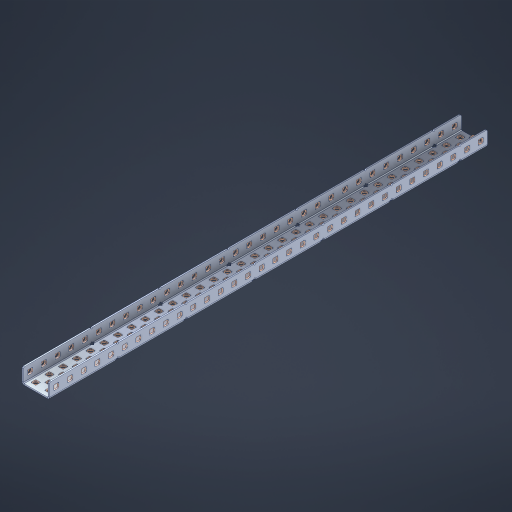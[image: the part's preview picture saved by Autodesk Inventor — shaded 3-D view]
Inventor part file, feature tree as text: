
AUTODESK INVENTOR PART (.ipt)
format: ipt  version: 2023 (Build 270158000, 158)  size: 1,968,128 bytes
history: native  units: in
note: dims shown in document units (in); Inventor stores cm internally (conversion verified against a paired STEP export)
features: other x167, extrude x158, sheet_metal_op x11, sketch x10, pattern_linear x2, mirror x1, chamfer x1
ambient origin geometry x8: Origin, YZ Plane, XZ Plane, XY Plane, X Axis, Y Axis, Z Axis, Center Point
bodies: Solid1 (feature_tree), Body (feature_tree)
feature tree (350):
  sheet_metal_op  "Flanges"
  other  "Flange Pattern Plane"
  other  "Flange Pattern Sketch"
  sheet_metal_op  "Flange Pattern"
  sheet_metal_op  "Body Pattern"
  pattern_linear  "Center Pattern"  Spacing1=0.0469in  [1 undecoded]
  other  "Arc Length"
  mirror  "Notch Mirror"
  pattern_linear  "Notch Pattern"  Spacing1=0.182in  [1 undecoded]
  chamfer  "End Chamfer"
  extrude  "Half Cut"  Depth=0.02in
  sketch  "Sketch1"  dims[d0=1.0in]
  other  "Plate1"
  sketch  "Sketch2"  dims[d1=16.0in]
  other  "Plate2"
  sheet_metal_op  "Bend1"
  sheet_metal_op  "Corner1"
  sketch  "Sketch3"  dims[d2=0.0469in]
  sketch  "Sketch7"  dims[d3=0.0469in]
  other  "Srf1"
  other  "Srf2"
  sketch  "Sketch8"  dims[d4=0.0234in]
  sketch  "Sketch9"  dims[d5=0.0938in]
  other  "Srf91"
  sheet_metal_op  "Body Pattern Sketch"
  other  "Srf92"
  sketch  "Sketch13"  dims[d6=0.0469in]
  sketch  "Sketch14"  dims[d7=0.5in d8=90.0deg d9=0.0312in]
  sketch  "Sketch15"  dims[d10=0.1875in]
  sketch  "Sketch16"  dims[d11=0.0469in d12=0.0469in d16=0.182in d17=0.02in d18=0.0469in d19=0.0in d20=0.25in d21=0.25in d38=12.5984in d40=0.5in d41=0.7874in d43=1.0in d46=0.172in d47=1.0in d48=0.0in d49=0.182in d50=0.02in d51=0.25in d52=0.25in d53=0.0469in d54=0.0in d55=0.172in d56=1.0in d57=0.0in d58=0.25in d60=12.5984in d62=0.5in d63=0.7874in d65=0.5in d85=0.1227in d86=0.1659in d88=0.04in d89=0.0469in d90=0.0in d91=0.04in d92=0.0491in d95=2.5in d96=0.04in d97=0.25in d98=45.0deg d99=0.25in d100=0.5in d101=0.0in d102=2.497in d106=0.182in d107=0.02in d108=0.5in d109=0.5in d110=0.0469in d111=0.0in d112=0.172in d113=0.5in d114=0.0in d117=0.5in d118=0.5in d119=0.5in]
  other  "Srf786"
  other  "Srf823"
  other  "Srf824"
  other  "Srf825"
  other  "Srf826"
  other  "Srf827"
  other  "Srf828"
  other  "Srf829"
  other  "Srf856"
  other  "Srf857"
  other  "Srf858"
  other  "Srf859"
  other  "Srf860"
  other  "Srf861"
  other  "Srf862"
  other  "Srf889"
  other  "Srf890"
  other  "Srf891"
  other  "Srf892"
  other  "Srf893"
  other  "Srf894"
  other  "Srf895"
  other  "Srf896"
  other  "Srf922"
  other  "Srf923"
  other  "Srf924"
  other  "Srf925"
  other  "Srf926"
  other  "Srf959"
  other  "Srf960"
  other  "Srf961"
  other  "Srf962"
  other  "Srf963"
  other  "Srf996"
  other  "Srf997"
  other  "Srf998"
  other  "Srf999"
  other  "Srf1000"
  other  "Srf1143"
  other  "Srf1144"
  other  "Srf1145"
  other  "Srf1146"
  other  "Srf1147"
  other  "Srf1148"
  other  "Srf1149"
  other  "Srf1150"
  other  "Srf1151"
  other  "Srf1152"
  other  "Srf1153"
  other  "Srf1154"
  other  "Srf1155"
  other  "Srf1156"
  other  "Srf1157"
  other  "Srf1158"
  other  "Srf1159"
  other  "Srf1160"
  other  "Srf1161"
  other  "Srf1162"
  other  "Srf1163"
  other  "Srf1164"
  other  "Srf1165"
  other  "Srf1166"
  other  "Srf1167"
  other  "Srf1168"
  other  "Srf1169"
  other  "Srf1170"
  other  "Srf1171"
  other  "Srf1172"
  other  "Srf1173"
  other  "Srf1174"
  other  "Srf1175"
  other  "Srf1176"
  other  "Srf1177"
  other  "Srf1178"
  other  "Srf1179"
  other  "Srf1180"
  other  "Srf1181"
  other  "Srf1182"
  other  "Srf1183"
  other  "Srf1184"
  other  "Srf1185"
  other  "Srf1186"
  other  "Srf1187"
  other  "Srf1188"
  other  "Srf1189"
  other  "Srf1190"
  other  "Srf1191"
  other  "Srf1192"
  other  "Srf1199"
  other  "Srf1200"
  other  "Srf1201"
  other  "Srf1202"
  other  "Srf1203"
  other  "Srf1204"
  other  "Srf1205"
  other  "Srf1206"
  other  "Srf1207"
  other  "Srf1208"
  other  "Srf1209"
  other  "Srf1210"
  other  "Srf1211"
  other  "Srf1212"
  other  "Srf1213"
  other  "Srf1214"
  other  "Srf1215"
  other  "Srf1216"
  other  "Srf1217"
  other  "Srf1218"
  other  "Srf1219"
  other  "Srf1220"
  other  "Srf1221"
  other  "Srf1222"
  other  "Srf1223"
  other  "Srf1224"
  other  "Srf1225"
  other  "Srf1226"
  other  "Srf1227"
  other  "Srf1228"
  other  "Srf1229"
  other  "Srf1230"
  other  "Srf1231"
  other  "Srf1232"
  other  "Srf1233"
  other  "Srf1234"
  other  "Srf1235"
  other  "Srf1236"
  other  "Srf1237"
  other  "Srf1238"
  other  "Srf1239"
  other  "Srf1240"
  other  "Srf1241"
  other  "Srf1242"
  other  "Srf1243"
  other  "Srf1244"
  other  "Srf1245"
  other  "Srf1246"
  other  "Srf1247"
  other  "Srf1248"
  other  "Srf1255"
  other  "Srf1256"
  other  "Srf1257"
  other  "Srf1258"
  other  "Srf1259"
  other  "Srf1260"
  other  "Srf1261"
  other  "Srf1262"
  other  "Srf1263"
  other  "Srf1264"
  other  "Srf1265"
  other  "Srf1266"
  other  "Srf1267"
  other  "Srf1268"
  other  "Srf1269"
  other  "Srf1270"
  other  "Srf1271"
  other  "Srf1272"
  sheet_metal_op  "Flange Stamp"
  sheet_metal_op  "Flange Circle"
  sheet_metal_op  "Body Stamp"
  sheet_metal_op  "Body Circle"
  other  "Center Stamp"
  other  "Center Circle"
  sheet_metal_op  "Notch"
  extrude  "ExtrusionSrf2"  Depth=0.0469in
  extrude  "ExtrusionSrf92"  TaperAngle=0.0deg  [1 undecoded]
  extrude  "ExtrusionSrf823"  Depth=0.5in
  extrude  "ExtrusionSrf824"  Depth=0.5in
  extrude  "ExtrusionSrf825"  Depth=0.5in
  extrude  "ExtrusionSrf826"  Depth=0.5in
  extrude  "ExtrusionSrf827"  Depth=1.0in TaperAngle=0.0deg
  extrude  "ExtrusionSrf828"  Depth=0.5in
  extrude  "ExtrusionSrf829"  Depth=0.02in
  extrude  "ExtrusionSrf856"  Depth=0.5in
  extrude  "ExtrusionSrf857"  Depth=0.5in
  extrude  "ExtrusionSrf858"  Depth=0.0469in
  extrude  "ExtrusionSrf859"  TaperAngle=0.0deg  [1 undecoded]
  extrude  "ExtrusionSrf860"  Depth=0.5in
  extrude  "ExtrusionSrf861"  Depth=1.0in TaperAngle=0.0deg
  extrude  "ExtrusionSrf862"  Depth=0.5in
  extrude  "ExtrusionSrf889"  Depth=0.5in
  extrude  "ExtrusionSrf890"  Depth=0.5in
  extrude  "ExtrusionSrf891"  Depth=0.5in
  extrude  "ExtrusionSrf892"  Depth=0.5in
  extrude  "ExtrusionSrf893"  Depth=0.5in
  extrude  "ExtrusionSrf894"  Depth=0.0469in
  extrude  "ExtrusionSrf895"  TaperAngle=0.0deg  [1 undecoded]
  extrude  "ExtrusionSrf896"  Depth=0.5in
  extrude  "ExtrusionSrf922"  Depth=0.5in
  extrude  "ExtrusionSrf923"  Depth=2.5in
  extrude  "ExtrusionSrf924"  Depth=0.5in TaperAngle=45.0deg
  extrude  "ExtrusionSrf925"  Depth=0.5in
  extrude  "ExtrusionSrf926"  Depth=0.5in TaperAngle=0.0deg
  extrude  "ExtrusionSrf959"  Depth=0.5in
  extrude  "ExtrusionSrf960"  Depth=0.5in
  extrude  "ExtrusionSrf961"  Depth=0.02in
  extrude  "ExtrusionSrf962"  Depth=0.5in
  extrude  "ExtrusionSrf963"  Depth=0.5in
  extrude  "ExtrusionSrf996"  Depth=0.0469in
  extrude  "ExtrusionSrf997"  TaperAngle=0.0deg  [1 undecoded]
  extrude  "ExtrusionSrf998"  Depth=0.5in
  extrude  "ExtrusionSrf999"  Depth=0.5in TaperAngle=0.0deg
  extrude  "ExtrusionSrf1000"  Depth=0.5in
  extrude  "ExtrusionSrf1143"  Depth=0.5in
  extrude  "ExtrusionSrf1144"  Depth=0.5in
  extrude  "ExtrusionSrf1145"  [1 undecoded]
  extrude  "ExtrusionSrf1146"  [1 undecoded]
  extrude  "ExtrusionSrf1147"  [1 undecoded]
  extrude  "ExtrusionSrf1148"  [1 undecoded]
  extrude  "ExtrusionSrf1149"  [1 undecoded]
  extrude  "ExtrusionSrf1150"  [1 undecoded]
  extrude  "ExtrusionSrf1151"  [1 undecoded]
  extrude  "ExtrusionSrf1152"  [1 undecoded]
  extrude  "ExtrusionSrf1153"  [1 undecoded]
  extrude  "ExtrusionSrf1154"  [1 undecoded]
  extrude  "ExtrusionSrf1155"  [1 undecoded]
  extrude  "ExtrusionSrf1156"  [1 undecoded]
  extrude  "ExtrusionSrf1157"  [1 undecoded]
  extrude  "ExtrusionSrf1158"  [1 undecoded]
  extrude  "ExtrusionSrf1159"  [1 undecoded]
  extrude  "ExtrusionSrf1160"  [1 undecoded]
  extrude  "ExtrusionSrf1161"  [1 undecoded]
  extrude  "ExtrusionSrf1162"  [1 undecoded]
  extrude  "ExtrusionSrf1163"  [1 undecoded]
  extrude  "ExtrusionSrf1164"  [1 undecoded]
  extrude  "ExtrusionSrf1165"  [1 undecoded]
  extrude  "ExtrusionSrf1166"  [1 undecoded]
  extrude  "ExtrusionSrf1167"  [1 undecoded]
  extrude  "ExtrusionSrf1168"  [1 undecoded]
  extrude  "ExtrusionSrf1169"  [1 undecoded]
  extrude  "ExtrusionSrf1170"  [1 undecoded]
  extrude  "ExtrusionSrf1171"  [1 undecoded]
  extrude  "ExtrusionSrf1172"  [1 undecoded]
  extrude  "ExtrusionSrf1173"  [1 undecoded]
  extrude  "ExtrusionSrf1174"  [1 undecoded]
  extrude  "ExtrusionSrf1175"  [1 undecoded]
  extrude  "ExtrusionSrf1176"  [1 undecoded]
  extrude  "ExtrusionSrf1177"  [1 undecoded]
  extrude  "ExtrusionSrf1178"  [1 undecoded]
  extrude  "ExtrusionSrf1179"  [1 undecoded]
  extrude  "ExtrusionSrf1180"  [1 undecoded]
  extrude  "ExtrusionSrf1181"  [1 undecoded]
  extrude  "ExtrusionSrf1182"  [1 undecoded]
  extrude  "ExtrusionSrf1183"  [1 undecoded]
  extrude  "ExtrusionSrf1184"  [1 undecoded]
  extrude  "ExtrusionSrf1185"  [1 undecoded]
  extrude  "ExtrusionSrf1186"  [1 undecoded]
  extrude  "ExtrusionSrf1187"  [1 undecoded]
  extrude  "ExtrusionSrf1188"  [1 undecoded]
  extrude  "ExtrusionSrf1189"  [1 undecoded]
  extrude  "ExtrusionSrf1190"  [1 undecoded]
  extrude  "ExtrusionSrf1191"  [1 undecoded]
  extrude  "ExtrusionSrf1192"  [1 undecoded]
  extrude  "ExtrusionSrf1199"  [1 undecoded]
  extrude  "ExtrusionSrf1200"  [1 undecoded]
  extrude  "ExtrusionSrf1201"  [1 undecoded]
  extrude  "ExtrusionSrf1202"  [1 undecoded]
  extrude  "ExtrusionSrf1203"  [1 undecoded]
  extrude  "ExtrusionSrf1204"  [1 undecoded]
  extrude  "ExtrusionSrf1205"  [1 undecoded]
  extrude  "ExtrusionSrf1206"  [1 undecoded]
  extrude  "ExtrusionSrf1207"  [1 undecoded]
  extrude  "ExtrusionSrf1208"  [1 undecoded]
  extrude  "ExtrusionSrf1209"  [1 undecoded]
  extrude  "ExtrusionSrf1210"  [1 undecoded]
  extrude  "ExtrusionSrf1211"  [1 undecoded]
  extrude  "ExtrusionSrf1212"  [1 undecoded]
  extrude  "ExtrusionSrf1213"  [1 undecoded]
  extrude  "ExtrusionSrf1214"  [1 undecoded]
  extrude  "ExtrusionSrf1215"  [1 undecoded]
  extrude  "ExtrusionSrf1216"  [1 undecoded]
  extrude  "ExtrusionSrf1217"  [1 undecoded]
  extrude  "ExtrusionSrf1218"  [1 undecoded]
  extrude  "ExtrusionSrf1219"  [1 undecoded]
  extrude  "ExtrusionSrf1220"  [1 undecoded]
  extrude  "ExtrusionSrf1221"  [1 undecoded]
  extrude  "ExtrusionSrf1222"  [1 undecoded]
  extrude  "ExtrusionSrf1223"  [1 undecoded]
  extrude  "ExtrusionSrf1224"  [1 undecoded]
  extrude  "ExtrusionSrf1225"  [1 undecoded]
  extrude  "ExtrusionSrf1226"  [1 undecoded]
  extrude  "ExtrusionSrf1227"  [1 undecoded]
  extrude  "ExtrusionSrf1228"  [1 undecoded]
  extrude  "ExtrusionSrf1229"  [1 undecoded]
  extrude  "ExtrusionSrf1230"  [1 undecoded]
  extrude  "ExtrusionSrf1231"  [1 undecoded]
  extrude  "ExtrusionSrf1232"  [1 undecoded]
  extrude  "ExtrusionSrf1233"  [1 undecoded]
  extrude  "ExtrusionSrf1234"  [1 undecoded]
  extrude  "ExtrusionSrf1235"  [1 undecoded]
  extrude  "ExtrusionSrf1236"  [1 undecoded]
  extrude  "ExtrusionSrf1237"  [1 undecoded]
  extrude  "ExtrusionSrf1238"  [1 undecoded]
  extrude  "ExtrusionSrf1239"  [1 undecoded]
  extrude  "ExtrusionSrf1240"  [1 undecoded]
  extrude  "ExtrusionSrf1241"  [1 undecoded]
  extrude  "ExtrusionSrf1242"  [1 undecoded]
  extrude  "ExtrusionSrf1243"  [1 undecoded]
  extrude  "ExtrusionSrf1244"  [1 undecoded]
  extrude  "ExtrusionSrf1245"  [1 undecoded]
  extrude  "ExtrusionSrf1246"  [1 undecoded]
  extrude  "ExtrusionSrf1247"  [1 undecoded]
  extrude  "ExtrusionSrf1248"  [1 undecoded]
  extrude  "ExtrusionSrf1255"  [1 undecoded]
  extrude  "ExtrusionSrf1256"  [1 undecoded]
  extrude  "ExtrusionSrf1257"  [1 undecoded]
  extrude  "ExtrusionSrf1258"  [1 undecoded]
  extrude  "ExtrusionSrf1259"  [1 undecoded]
  extrude  "ExtrusionSrf1260"  [1 undecoded]
  extrude  "ExtrusionSrf1261"  [1 undecoded]
  extrude  "ExtrusionSrf1262"  [1 undecoded]
  extrude  "ExtrusionSrf1263"  [1 undecoded]
  extrude  "ExtrusionSrf1264"  [1 undecoded]
  extrude  "ExtrusionSrf1265"  [1 undecoded]
  extrude  "ExtrusionSrf1266"  [1 undecoded]
  extrude  "ExtrusionSrf1267"  [1 undecoded]
  extrude  "ExtrusionSrf1268"  [1 undecoded]
  extrude  "ExtrusionSrf1269"  [1 undecoded]
  extrude  "ExtrusionSrf1270"  [1 undecoded]
  extrude  "ExtrusionSrf1271"  [1 undecoded]
  extrude  "ExtrusionSrf1272"  [1 undecoded]
note: 122 required parameter values undecoded (feature->parameter linkage not recoverable at this tier; creation-order binding heuristic only, values carry confidence <= 0.55)
